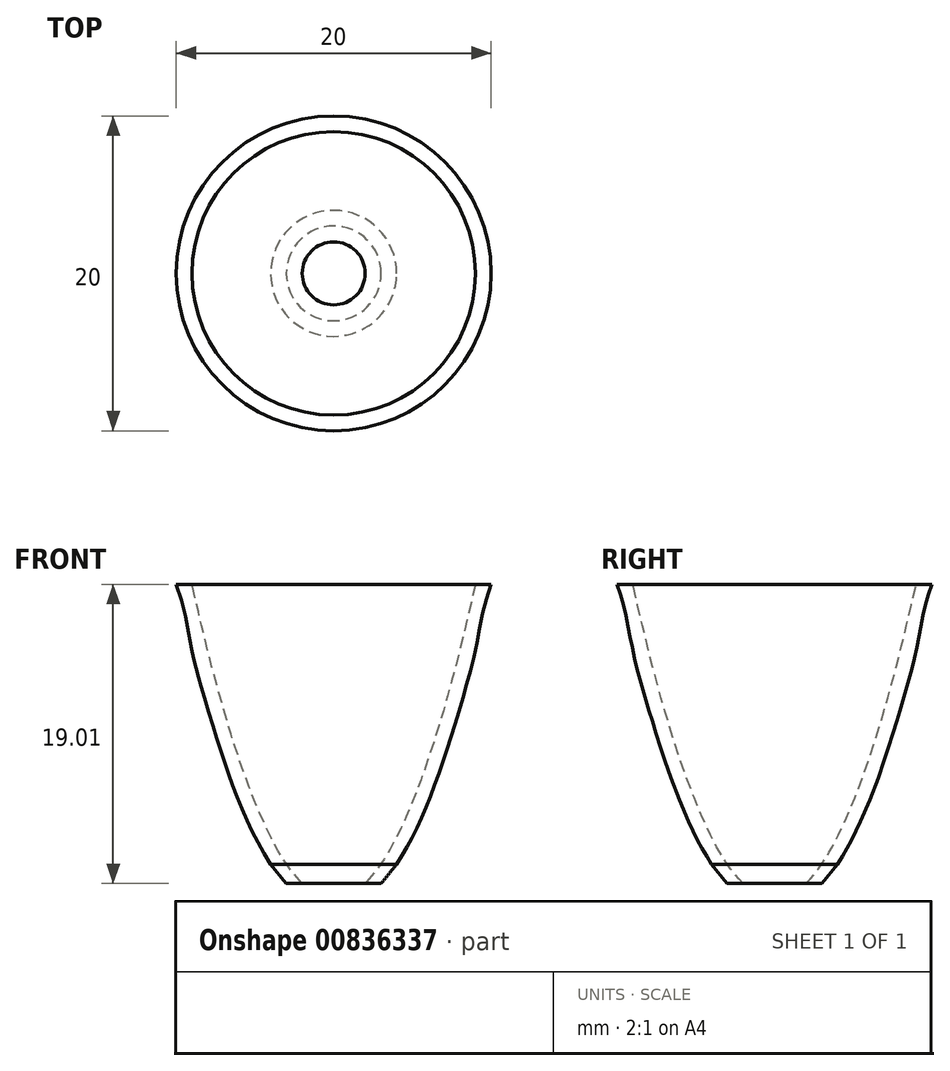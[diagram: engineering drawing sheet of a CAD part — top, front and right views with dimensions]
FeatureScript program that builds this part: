
annotation { "Feature Type Name" : "Feature", "Feature Type Description" : "" }
export const myFeature = defineFeature(function(context is Context, id is Id, definition is map)
    precondition{}
    {
        {
            var Q0;
            Q0=qCreatedBy(makeId("Front.planeOp"),FACE);
            var sketch = newSketch(context, id + "F0", { "sketchPlane" : qUnion([Q0])});
            skPoint(sketch, "E0", {"position": v(-9, 20) * mm});
            skPoint(sketch, "E1", {"position": v(-5, 6.17) * mm});
            skPoint(sketch, "E2", {"position": v(-2, 0.99) * mm});
            skPoint(sketch, "E3", {"position": v(-7, 12.1) * mm});
            skPoint(sketch, "E4", {"position": v(-8, 15.8) * mm});
            skPoint(sketch, "E5", {"position": v(-6, 8.89) * mm});
            skPoint(sketch, "E6", {"position": v(-4, 3.95) * mm});
            skPoint(sketch, "E7", {"position": v(-3, 2.22) * mm});
            skFitSpline(sketch, "E8", {"points": [v(-9, 20) * mm, v(-8, 15.8) * mm, v(-7, 12.1) * mm, v(-6, 8.89) * mm, v(-5, 6.17) * mm, v(-4, 3.95) * mm, v(-3, 2.22) * mm, v(-2, 0.99) * mm], "startDerivative": vector(5.61, -24.18) * mm, "endDerivative": vector(9.58, -10.96) * mm});
            skPoint(sketch, "E9", {"position": v(-10, 20) * mm});
            skFitSpline(sketch, "E10", {"points": [v(-10, 20) * mm, v(-9, 15.8) * mm, v(-8, 12.1) * mm, v(-7, 8.89) * mm, v(-6, 6.17) * mm, v(-5, 3.95) * mm, v(-4, 2.22) * mm], "startDerivative": vector(8.12, -21.23) * mm, "endDerivative": vector(7.63, -12.5) * mm});
            skLineSegment(sketch, "E11", {"start": v(-10, 20) * mm, "end": v(-9, 20) * mm});
            skPoint(sketch, "E12", {"position": v(-3.01, 0.99) * mm});
            skFitSpline(sketch, "E13", {"points": [v(-4, 2.22) * mm, v(-3.01, 0.99) * mm], "startDerivative": vector(0.99, -1.23) * mm, "endDerivative": vector(0.99, -1.23) * mm});
            skLineSegment(sketch, "E14", {"start": v(-3.01, 0.99) * mm, "end": v(-2, 0.99) * mm});
            skLineSegment(sketch, "E15", {"start": v(0, 34.9) * mm, "end": v(0, -4.8) * mm, "construction": true});
            skSolve(sketch);
        }
        {
            var Q0;
            Q0 = qSketchRegion(id + "F0", true);
            var Q1;
            Q1=sQuery(id+"F0.wireOp",EDGE,"E15");
            revolve(context, id + "F1", {"surfaceOperationType" : NewSurfaceOperationType.NEW, "entities" : qUnion([Q0]), "axis" : qUnion([Q1]), "revolveType" : RevolveType.FULL});
        }
    });
